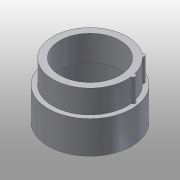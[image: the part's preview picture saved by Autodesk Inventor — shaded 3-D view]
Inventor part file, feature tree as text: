
AUTODESK INVENTOR PART (.ipt)
format: ipt  version: 2016 (Build 200138000, 138)  size: 126,464 bytes
history: native  units: mm
features: sketch x2, revolve x1, extrude x1
ambient origin geometry x8: Origin, YZ Plane, XZ Plane, XY Plane, X Axis, Y Axis, Z Axis, Center Point
bodies: Body1 (feature_tree)
feature tree (4):
  revolve  "Revolution1"  [1 undecoded]
  extrude  "Extrusion4"  TaperAngle=0.0deg  [1 undecoded]
  sketch  "Sketch4"  dims[d9=18.0mm d10=16.0mm]
  sketch  "Sketch5"  dims[d13=7.0mm d14=0.0mm d15=5.0mm d16=6.5mm d17=13.0mm d18=16.0mm d19=90.0deg d20=1.745329mm d21=6.981317mm d22=1.0mm d23=1.0mm d24=5.0mm d25=0.0mm]
note: 2 required parameter values undecoded (feature->parameter linkage not recoverable at this tier; creation-order binding heuristic only, values carry confidence <= 0.55)